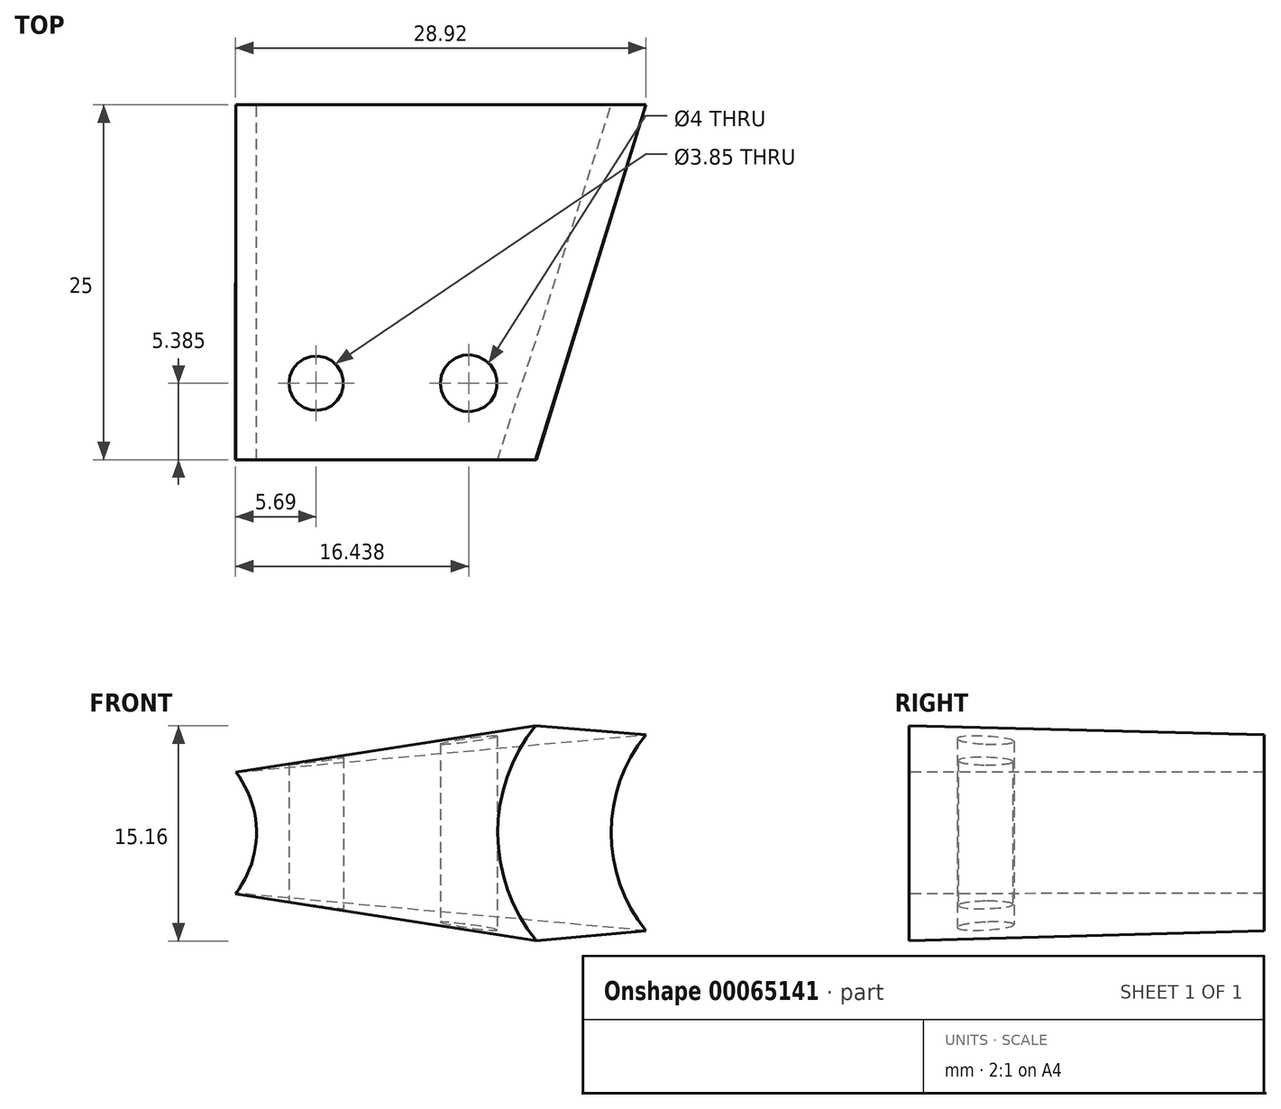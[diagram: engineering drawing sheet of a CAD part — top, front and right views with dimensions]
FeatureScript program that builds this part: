
annotation { "Feature Type Name" : "Feature", "Feature Type Description" : "" }
export const myFeature = defineFeature(function(context is Context, id is Id, definition is map)
    precondition{}
    {
        {
            var Q0;
            Q0=qCreatedBy(makeId("Front.planeOp"),FACE);
            var sketch = newSketch(context, id + "F0", { "sketchPlane" : qUnion([Q0])});
            skArc(sketch, "E0", {"start": v(-15.95, -4.26) * mm, "mid": v(-14.5, 0) * mm, "end": v(-15.95, 4.26) * mm});
            skArc(sketch, "E1", {"start": v(12.94, 6.9) * mm, "mid": v(10.5, 0) * mm, "end": v(12.94, -6.9) * mm});
            skLineSegment(sketch, "E2", {"start": v(-15.95, 4.26) * mm, "end": v(12.94, 6.9) * mm});
            skLineSegment(sketch, "E3", {"start": v(12.94, -6.9) * mm, "end": v(-15.95, -4.26) * mm});
            skSolve(sketch);
        }
        {
            var Q0;
            Q0=qCreatedBy(makeId("Front.planeOp"),FACE);
            var sketch = newSketch(context, id + "F1", { "sketchPlane" : qUnion([Q0])});
            skLineSegment(sketch, "E4.bottom", {"start": v(-5.96, 3.01) * mm, "end": v(-0.1, 3.01) * mm});
            skLineSegment(sketch, "E4.top", {"start": v(-5.96, -3.28) * mm, "end": v(-0.1, -3.28) * mm});
            skLineSegment(sketch, "E4.left", {"start": v(-5.96, 3.01) * mm, "end": v(-5.96, -3.28) * mm});
            skLineSegment(sketch, "E4.right", {"start": v(-0.1, 3.01) * mm, "end": v(-0.1, -3.28) * mm});
            skSolve(sketch);
        }
        {
            var Q0;
            Q0=makeQuery(id+"F1.imprint","IMPRINT",FACE,{"disambiguationData":[TD([[makeQuery(id+"F1.imprint","IMPRINT",EDGE,{"derivedFrom":sQuery(id+"F1.wireOp",EDGE,"E4.bottom")}),-1.0]])]});
            extrude(context, id + "F2", {"entities" : qUnion([Q0]), "depth" : 25 * mm});
        }
        {
            var Q0;
            Q0=makeQuery(id+"F2.opExtrude","CAP_FACE",FACE,{"disambiguationData":[OSD([sQuery(id+"F1.wireOp",EDGE,"E4.bottom"),sQuery(id+"F1.wireOp",EDGE,"E4.top"),sQuery(id+"F1.wireOp",EDGE,"E4.left"),sQuery(id+"F1.wireOp",EDGE,"E4.right")])],"isStart":false});
            var sketch = newSketch(context, id + "F3", { "sketchPlane" : qUnion([Q0])});
            skArc(sketch, "E5", {"start": v(-15.98, -4.3) * mm, "mid": v(-14.5, -0.03) * mm, "end": v(-15.95, 4.26) * mm});
            skArc(sketch, "E6", {"start": v(5.16, 7.53) * mm, "mid": v(2.5, -0.06) * mm, "end": v(5.23, -7.63) * mm});
            skLineSegment(sketch, "E7", {"start": v(-15.95, 4.26) * mm, "end": v(5.16, 7.53) * mm});
            skLineSegment(sketch, "E8", {"start": v(5.23, -7.63) * mm, "end": v(-15.98, -4.3) * mm});
            skSolve(sketch);
        }
        {
            var Q1;
            Q1 = qSketchRegion(id + "F0", true);
            var Q2;
            Q2 = qSketchRegion(id + "F3", true);
            loft(context, id + "F4", {"operationType" : NewBodyOperationType.ADD, "sheetProfilesArray" : [{ "sheetProfileEntities" : qUnion([Q1]) }, { "sheetProfileEntities" : qUnion([Q2]) }]});
        }
        {
            var Q0;
            Q0=qCreatedBy(makeId("Top.planeOp"),FACE);
            var sketch = newSketch(context, id + "F5", { "sketchPlane" : qUnion([Q0])});
            skCircle(sketch, "E9", {"center": v(-10.3, -19.61) * mm, "radius": 1.92 * mm});
            skCircle(sketch, "E10", {"center": v(0.46, -19.61) * mm, "radius": 2 * mm});
            skSolve(sketch);
        }
        {
            var Q0;
            Q0=makeQuery(id+"F5.imprint","IMPRINT",FACE,{"disambiguationData":[TD([[makeQuery(id+"F5.imprint","IMPRINT",EDGE,{"derivedFrom":sQuery(id+"F5.wireOp",EDGE,"E9")}),1.0]])]});
            var Q1;
            Q1=makeQuery(id+"F5.imprint","IMPRINT",FACE,{"disambiguationData":[TD([[makeQuery(id+"F5.imprint","IMPRINT",EDGE,{"derivedFrom":sQuery(id+"F5.wireOp",EDGE,"E10")}),1.0]])]});
            extrude(context, id + "F6", {"entities" : qUnion([Q0, Q1]), "operationType" : NewBodyOperationType.REMOVE, "depth" : 10 * mm, "hasSecondDirection" : true, "secondDirectionOppositeDirection" : true, "secondDirectionDepth" : 10 * mm});
        }
    });
